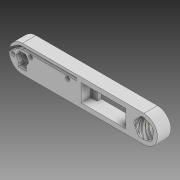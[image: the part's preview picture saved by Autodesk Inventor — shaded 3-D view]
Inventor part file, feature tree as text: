
AUTODESK INVENTOR PART (.ipt)
format: ipt  version: 2020 (Build 240168000, 168)  size: 822,272 bytes
history: native  units: mm
features: sketch x11, extrude x10, plane x2, fillet x2, other x1, helix x1, pattern_circular x1, projected_geometry x1
ambient origin geometry x8: Origin, YZ Plane, XZ Plane, XY Plane, X Axis, Y Axis, Z Axis, Center Point
bodies: Solid1 (feature_tree)
feature tree (29):
  extrude  "Extrusion1"  Depth=10.0mm
  extrude  "Extrusion2"  Depth=10.0mm
  extrude  "Extrusion4"  Depth=2.0mm
  extrude  "Extrusion5"  Depth=40.0mm
  plane  "Work Plane1"
  extrude  "Extrusion6"  Depth=13.0mm
  extrude  "Extrusion7"  Depth=15.0mm
  sketch  "Sketch8"  dims[d21=4.7mm]
  other  "Work Axis1"
  helix  "Coil1"  [1 undecoded]
  fillet  "Fillet1"  [1 undecoded]
  pattern_circular  "Circular Pattern1"  [2 undecoded]
  extrude  "Extrusion8"  Depth=10.0mm TaperAngle=0.0deg
  fillet  "Fillet2"  Radius=12.5mm
  extrude  "Extrusion9"  TaperAngle=0.0deg  [1 undecoded]
  plane  "Work Plane2"
  extrude  "Extrusion10"  Depth=10.0mm
  extrude  "Extrusion11"  Depth=10.0mm
  sketch  "Sketch1"  dims[d0=90.0mm d1=10.0mm]
  sketch  "Sketch2"  dims[d2=10.0mm d3=0.0mm d4=5.5mm]
  sketch  "Sketch4"  dims[d5=0.0mm d6=0.0mm d10=2.0mm]
  sketch  "Sketch5"  dims[d11=2.0mm d12=40.0mm]
  sketch  "Sketch6"  dims[d13=4.0mm d14=0.0mm d15=13.0mm]
  sketch  "Sketch7"  dims[d16=33.0mm d17=15.0mm d18=11.75mm d19=0.0mm d20=-2.0mm]
  sketch  "Sketch9"  dims[d22=4.7mm]
  sketch  "Sketch11"  dims[d23=2.5mm]
  sketch  "Sketch12"  dims[d24=2.5mm]
  sketch  "Sketch13"  dims[d25=3.0mm d26=3.0mm d27=2.0mm d28=0.0mm d29=12.5mm d30=0.0mm d31=0.0mm d34=25.0mm d35=10.0mm d36=10.0mm d37=0.0mm d38=90.0deg d39=90.0deg d40=0.0mm d41=0.0mm d43=1.5mm d44=0.75mm d45=0.5mm d46=50.0mm d47=360.0deg d49=8.0mm d50=3.0mm d51=2.0mm d52=2.0mm d53=3.0mm d56=7.0mm d57=0.0mm d58=0.5mm d59=6.0mm d60=3.3mm d61=10.0mm d62=0.0mm d63=-3.5mm d64=5.8mm d65=2.6mm d66=0.0mm d67=8.1mm d68=3.0mm d69=0.0mm d70=4.0mm d71=6.0mm d72=1.0mm d73=0.0mm d74=10.0mm]
  projected_geometry  "Projected Loop1"
note: 5 required parameter values undecoded (feature->parameter linkage not recoverable at this tier; creation-order binding heuristic only, values carry confidence <= 0.55)
